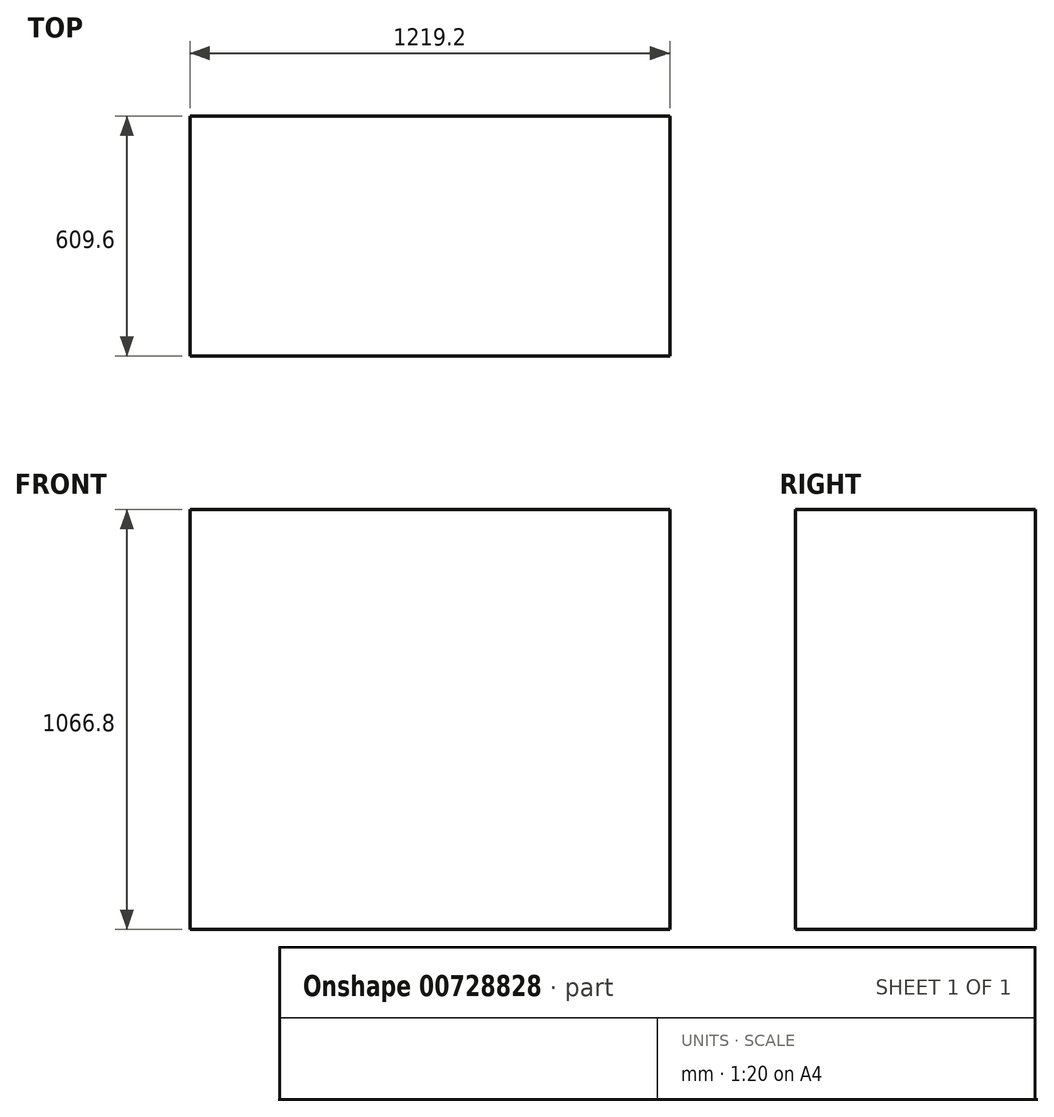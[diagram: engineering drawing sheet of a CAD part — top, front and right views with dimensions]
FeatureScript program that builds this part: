
annotation { "Feature Type Name" : "Feature", "Feature Type Description" : "" }
export const myFeature = defineFeature(function(context is Context, id is Id, definition is map)
    precondition{}
    {
        {
            var Q0;
            Q0=qCreatedBy(makeId("Front.planeOp"),FACE);
            var sketch = newSketch(context, id + "F0", { "sketchPlane" : qUnion([Q0])});
            skLineSegment(sketch, "E0.bottom", {"start": v(-610.53, 769.2) * mm, "end": v(608.67, 769.2) * mm});
            skLineSegment(sketch, "E0.top", {"start": v(-610.53, -297.6) * mm, "end": v(608.67, -297.6) * mm});
            skLineSegment(sketch, "E0.left", {"start": v(-610.53, 769.2) * mm, "end": v(-610.53, -297.6) * mm});
            skLineSegment(sketch, "E0.right", {"start": v(608.67, 769.2) * mm, "end": v(608.67, -297.6) * mm});
            skSolve(sketch);
        }
        {
            var Q0;
            Q0=makeQuery(id+"F0.imprint","IMPRINT",FACE,{"disambiguationData":[TD([[makeQuery(id+"F0.imprint","IMPRINT",EDGE,{"derivedFrom":sQuery(id+"F0.wireOp",EDGE,"E0.bottom")}),-1.0]])]});
            extrude(context, id + "F1", {"entities" : qUnion([Q0]), "depth" : 609.6 * mm, "offsetDistance" : 25.4 * mm});
        }
    });
